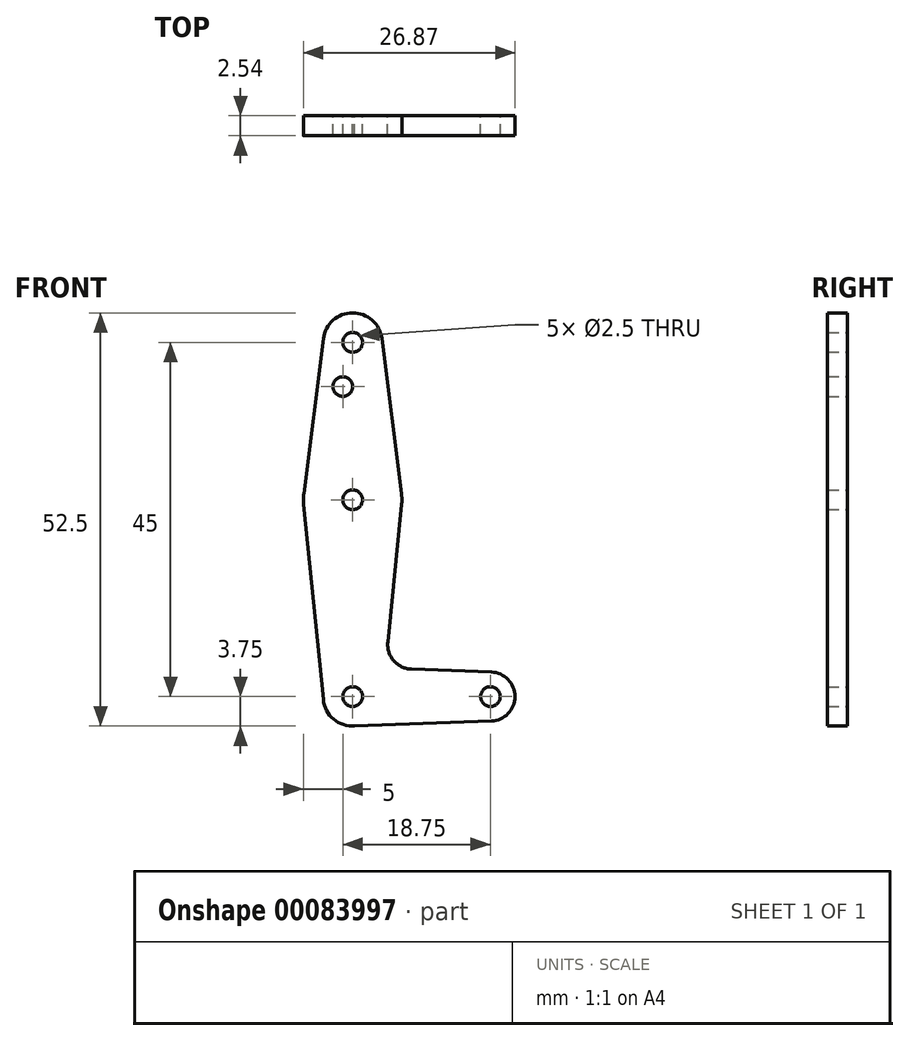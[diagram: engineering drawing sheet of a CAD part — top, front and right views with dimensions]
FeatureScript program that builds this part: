
annotation { "Feature Type Name" : "Feature", "Feature Type Description" : "" }
export const myFeature = defineFeature(function(context is Context, id is Id, definition is map)
    precondition{}
    {
        {
            var Q0;
            Q0=qCreatedBy(makeId("Front.planeOp"),FACE);
            var sketch = newSketch(context, id + "F0", { "sketchPlane" : qUnion([Q0])});
            skCircle(sketch, "E0", {"center": v(0, 0) * mm, "radius": 3.75 * mm});
            skCircle(sketch, "E1", {"center": v(0, 45) * mm, "radius": 3.75 * mm});
            skCircle(sketch, "E2", {"center": v(0, 25) * mm, "radius": 6.25 * mm});
            skCircle(sketch, "E3", {"center": v(17.5, 0) * mm, "radius": 3.12 * mm});
            skLineSegment(sketch, "E4", {"start": v(0, 0) * mm, "end": v(0, 45) * mm, "construction": true});
            skLineSegment(sketch, "E5", {"start": v(0, 0) * mm, "end": v(17.5, 0) * mm, "construction": true});
            skLineSegment(sketch, "E6", {"start": v(-6.2, 25.78) * mm, "end": v(-3.72, 45.47) * mm});
            skLineSegment(sketch, "E7", {"start": v(3.72, 45.47) * mm, "end": v(6.2, 25.78) * mm});
            skLineSegment(sketch, "E8", {"start": v(0, -3.75) * mm, "end": v(17.61, -3.12) * mm});
            skCircle(sketch, "E9", {"center": v(0, 45) * mm, "radius": 1.25 * mm});
            skCircle(sketch, "E10", {"center": v(0, 25) * mm, "radius": 1.25 * mm});
            skCircle(sketch, "E11", {"center": v(-1.25, 39.38) * mm, "radius": 1.25 * mm});
            skCircle(sketch, "E12", {"center": v(0, 0) * mm, "radius": 1.25 * mm});
            skCircle(sketch, "E13", {"center": v(17.5, 0) * mm, "radius": 1.25 * mm});
            skPoint(sketch, "E14.newPointA", {"position": v(3.77, 0) * mm});
            skLineSegment(sketch, "E15", {"start": v(4.47, 6.93) * mm, "end": v(6.22, 24.38) * mm});
            skLineSegment(sketch, "E16", {"start": v(17.61, 3.12) * mm, "end": v(7.47, 3.49) * mm});
            skLineSegment(sketch, "E17", {"start": v(-3.73, -0.38) * mm, "end": v(-6.22, 24.38) * mm});
            skPoint(sketch, "E18.newPointB", {"position": v(0, 3.75) * mm});
            skArc(sketch, "E18.filletArc", {"start": v(4.47, 6.93) * mm, "mid": v(5.22, 4.56) * mm, "end": v(7.47, 3.49) * mm});
            skSolve(sketch);
        }
        {
            var Q0;
            Q0 = qSketchRegion(id + "F0", true);
            extrude(context, id + "F1", {"entities" : qUnion([Q0]), "depth" : 2.54 * mm});
        }
    });
